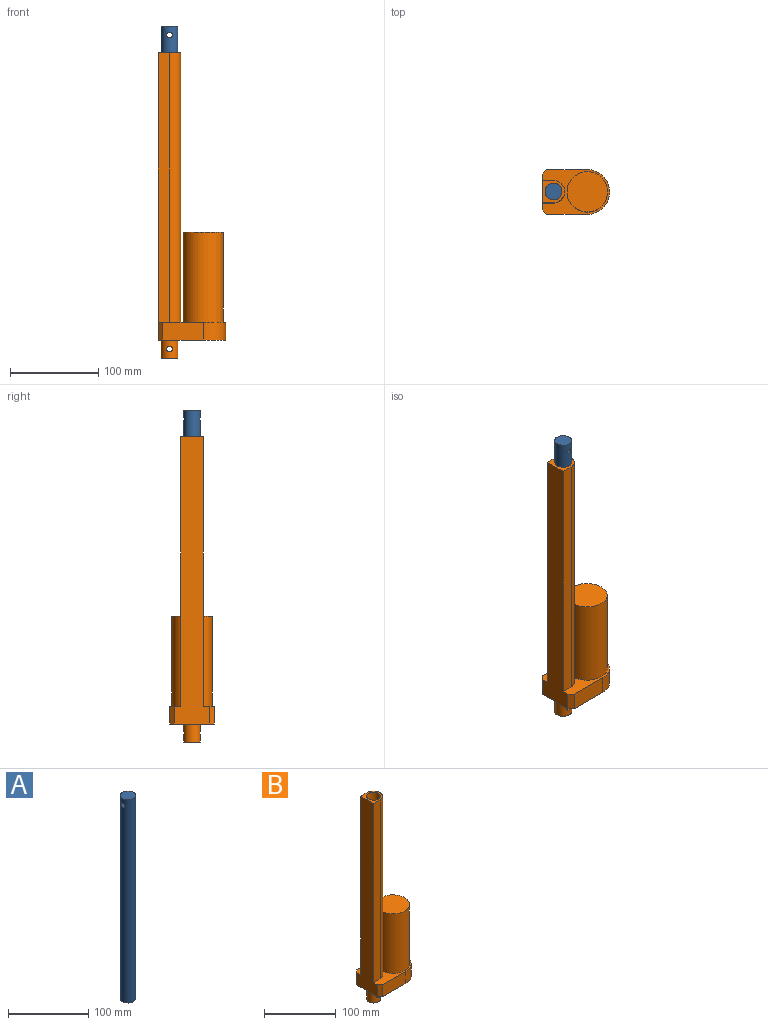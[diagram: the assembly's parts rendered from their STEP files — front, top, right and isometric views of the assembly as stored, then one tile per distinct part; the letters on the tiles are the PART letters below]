
ASSEMBLY  parts=2 mates=1
PART A: 4 faces, bbox 19.1x19.1x309.9 mm
  f0: cylinder r=9.53mm len=309.88mm, axis (0,0,-1), area 18481.3mm2, adj f1,f2,f3
  f1: plane 19.05x19.05mm, normal (0,0,1), area 285mm2, adj f0
  f2: plane 19.05x19.05mm, normal (0,0,-1), area 285mm2, adj f0
  f3: cylinder r=3.17mm len=19.05mm, axis (1,0,0), area 369.2mm2, adj f0
PART B: 19 faces, bbox 76.2x50.8x345.4 mm
  f0: plane 76.2x50.8mm, normal (0,0,1), area 1350.6mm2, adj f1,f2,f3,f4,f6,f8,f9,f10
  f1: plane 325.12x40.64mm, normal (-1,0,0), area 8567.7mm2, adj f0,f5,f8,f9,f10,f11,f12
  f2: plane 45.72x20.32mm, normal (0,-1,0), area 929mm2, adj f0,f3,f5,f9
  f3: cylinder r=25.4mm len=50.8mm, axis (0,0,-1), area 1621.5mm2, adj f0,f2,f4,f5
  f4: plane 45.72x20.32mm, normal (0,1,0), area 929mm2, adj f0,f3,f5,f8
  f5: plane 76.2x50.8mm, normal (0,0,-1), area 3283.2mm2, adj f1,f2,f3,f4,f8,f9,f16
  f6: cylinder r=22.86mm len=101.6mm, axis (0,0,-1), area 14593.2mm2, adj f0,f7
  f7: plane 45.72x45.72mm, normal (0,0,1), area 1641.7mm2, adj f6
  f8: plane 20.32x5.08mm, normal (-0.71,0.71,0), area 146mm2, adj f0,f1,f4,f5
  f9: plane 20.32x5.08mm, normal (-0.71,-0.71,0), area 146mm2, adj f0,f1,f2,f5
  f10: plane 304.8x12.7mm, normal (0,1,0), area 3871mm2, adj f0,f1,f12,f13
  f11: plane 304.8x12.7mm, normal (0,-1,0), area 3871mm2, adj f0,f1,f12,f13
  f12: plane 25.4x25.4mm, normal (0,0,1), area 290.9mm2, adj f1,f10,f11,f13,f14
  f13: cylinder r=12.7mm len=304.8mm, axis (0,0,-1), area 12161mm2, adj f0,f10,f11,f12
  f14: cylinder r=9.53mm len=254mm, axis (0,0,1), area 15201.2mm2, adj f12,f15
  f15: plane 19.05x19.05mm, normal (0,0,1), area 285mm2, adj f14
  f16: cylinder r=9.53mm len=20.32mm, axis (0,0,1), area 1151.8mm2, adj f5,f17,f18
  f17: plane 19.05x19.05mm, normal (0,0,-1), area 285mm2, adj f16
  f18: cylinder r=3.17mm len=19.05mm, axis (0,-1,0), area 369.2mm2, adj f16
PLACE A rot(axis=(0,0,1),90deg) t=(-25.16,0,45.72)mm
PLACE B t=(12.94,0,0)mm
MATE slider A.f0 <-> B.f14  axis (0,0,-1) through (-25.16,0,45.72)mm
